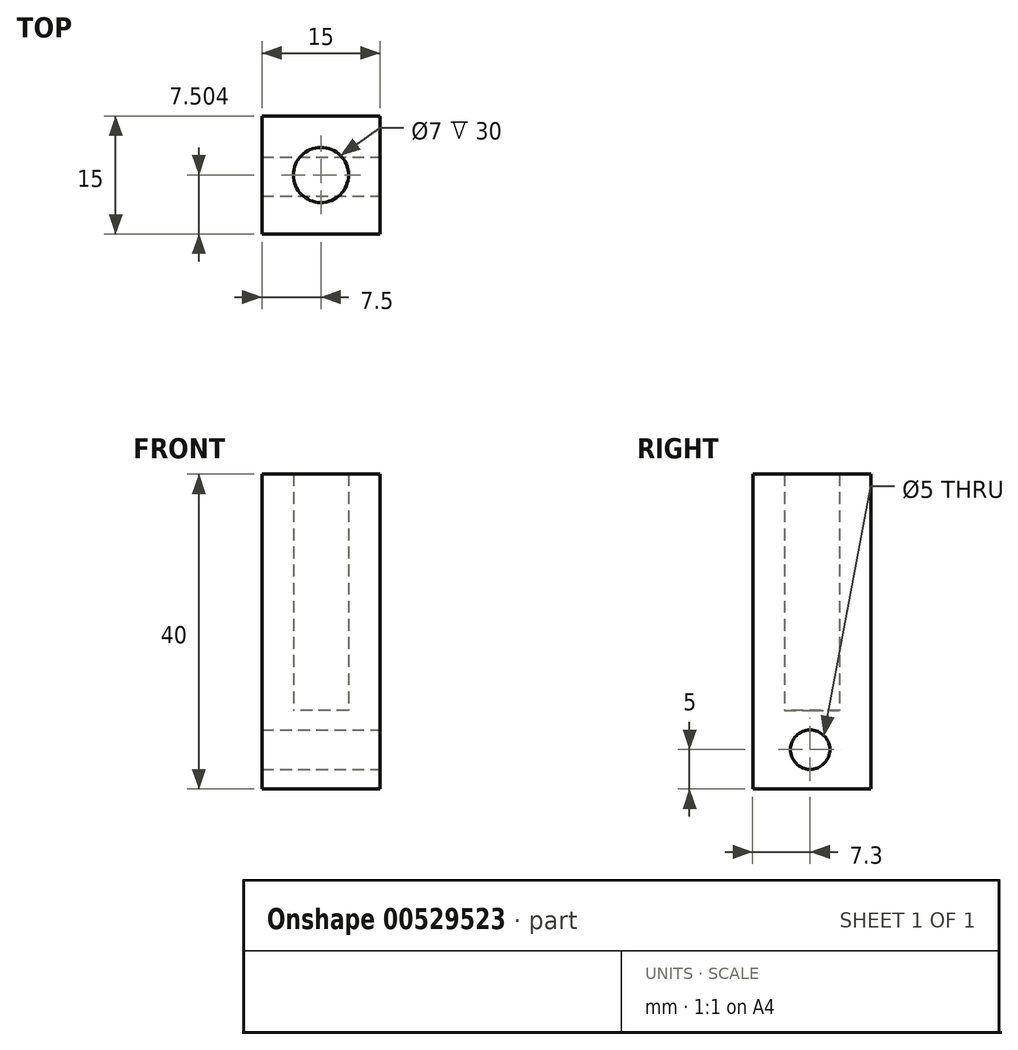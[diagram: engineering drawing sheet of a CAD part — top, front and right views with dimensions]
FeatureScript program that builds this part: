
annotation { "Feature Type Name" : "Feature", "Feature Type Description" : "" }
export const myFeature = defineFeature(function(context is Context, id is Id, definition is map)
    precondition{}
    {
        {
            var Q0;
            Q0=qCreatedBy(makeId("Top.planeOp"),FACE);
            var sketch = newSketch(context, id + "F0", { "sketchPlane" : qUnion([Q0])});
            skLineSegment(sketch, "E0.bottom", {"start": v(-7.5, 7.7) * mm, "end": v(7.5, 7.7) * mm});
            skLineSegment(sketch, "E0.top", {"start": v(-7.5, -7.3) * mm, "end": v(7.5, -7.3) * mm});
            skLineSegment(sketch, "E0.left", {"start": v(-7.5, 7.7) * mm, "end": v(-7.5, -7.3) * mm});
            skLineSegment(sketch, "E0.right", {"start": v(7.5, 7.7) * mm, "end": v(7.5, -7.3) * mm});
            skLineSegment(sketch, "E1", {"start": v(-7.5, -7.3) * mm, "end": v(-7.5, 0.2) * mm});
            skLineSegment(sketch, "E2", {"start": v(7.5, -7.3) * mm, "end": v(7.5, 0.2) * mm});
            skLineSegment(sketch, "E3", {"start": v(7.5, 0.2) * mm, "end": v(-7.5, 0.2) * mm});
            skLineSegment(sketch, "E4", {"start": v(-7.5, -7.3) * mm, "end": v(0, -7.3) * mm});
            skLineSegment(sketch, "E5", {"start": v(-7.5, 7.7) * mm, "end": v(0, 7.7) * mm});
            skLineSegment(sketch, "E6", {"start": v(0, 7.7) * mm, "end": v(0, -7.3) * mm});
            skCircle(sketch, "E7", {"center": v(0, 0.2) * mm, "radius": 3.5 * mm});
            skSolve(sketch);
        }
        {
            var Q0;
            {var subQ1=sQuery(id+"F0.wireOp",EDGE,"E0.bottom");Q0=makeQuery(id+"F0.imprint","IMPRINT",FACE,{"disambiguationData":[TD([[makeQuery(id+"F0.imprint","IMPRINT",EDGE,{"derivedFrom":subQ1}),-1.0]])]});}
            var Q1;
            {var subQ2=sQuery(id+"F0.wireOp",EDGE,"E0.left");Q1=makeQuery(id+"F0.imprint","IMPRINT",FACE,{"disambiguationData":[TD([[makeQuery(id+"F0.imprint","IMPRINT",EDGE,{"derivedFrom":subQ2}),1.0]])]});}
            var Q2;
            {var subQ4=sQuery(id+"F0.wireOp",EDGE,"E1");Q2=makeQuery(id+"F0.imprint","IMPRINT",FACE,{"disambiguationData":[TD([[makeQuery(id+"F0.imprint","IMPRINT",EDGE,{"derivedFrom":subQ4}),-1.0]])]});}
            var Q3;
            {var subQ1=sQuery(id+"F0.wireOp",EDGE,"E0.top");Q3=makeQuery(id+"F0.imprint","IMPRINT",FACE,{"disambiguationData":[TD([[makeQuery(id+"F0.imprint","IMPRINT",EDGE,{"derivedFrom":subQ1}),1.0]])]});}
            var Q4;
            {var subQ0=sQuery(id+"F0.wireOp",EDGE,"E6");var subQ1=sQuery(id+"F0.wireOp",EDGE,"E3");var subQ2=makeQuery(id+"F0.imprint","INTERSECT",VERTEX,{"derivedFrom":[subQ1,subQ0]});Q4=makeQuery(id+"F0.imprint","IMPRINT",FACE,{"disambiguationData":[TD([[makeQuery(id+"F0.imprint","IMPRINT",EDGE,{"disambiguationData":[TD([[subQ2,-1.0]])],"derivedFrom":subQ1}),-1.0]])]});}
            var Q5;
            {var subQ0=sQuery(id+"F0.wireOp",EDGE,"E7");var subQ1=sQuery(id+"F0.wireOp",EDGE,"E3");var subQ2=makeQuery(id+"F0.imprint","INTERSECT",VERTEX,{"disambiguationData":[OD(0.0)],"derivedFrom":[subQ1,subQ0]});Q5=makeQuery(id+"F0.imprint","IMPRINT",FACE,{"disambiguationData":[TD([[makeQuery(id+"F0.imprint","IMPRINT",EDGE,{"disambiguationData":[TD([[subQ2,-1.0]])],"derivedFrom":subQ1}),-1.0]])]});}
            var Q6;
            {var subQ0=sQuery(id+"F0.wireOp",EDGE,"E7");var subQ1=sQuery(id+"F0.wireOp",EDGE,"E3");var subQ2=makeQuery(id+"F0.imprint","INTERSECT",VERTEX,{"disambiguationData":[OD(0.0)],"derivedFrom":[subQ1,subQ0]});Q6=makeQuery(id+"F0.imprint","IMPRINT",FACE,{"disambiguationData":[TD([[makeQuery(id+"F0.imprint","IMPRINT",EDGE,{"disambiguationData":[TD([[subQ2,-1.0]])],"derivedFrom":subQ1}),1.0]])]});}
            var Q7;
            {var subQ0=sQuery(id+"F0.wireOp",EDGE,"E6");var subQ1=sQuery(id+"F0.wireOp",EDGE,"E3");var subQ2=makeQuery(id+"F0.imprint","INTERSECT",VERTEX,{"derivedFrom":[subQ1,subQ0]});Q7=makeQuery(id+"F0.imprint","IMPRINT",FACE,{"disambiguationData":[TD([[makeQuery(id+"F0.imprint","IMPRINT",EDGE,{"disambiguationData":[TD([[subQ2,-1.0]])],"derivedFrom":subQ1}),1.0]])]});}
            extrude(context, id + "F1", {"entities" : qUnion([Q0, Q1, Q2, Q3, Q4, Q5, Q6, Q7]), "depth" : 10 * mm, "offsetDistance" : 25 * mm});
        }
        {
            var Q0;
            Q0 = qSketchRegion(id + "F0", true);
            extrude(context, id + "F2", {"entities" : qUnion([Q0]), "operationType" : NewBodyOperationType.ADD, "depth" : 40 * mm, "offsetDistance" : 25 * mm});
        }
        {
            var Q0;
            {var subQ0=sQuery(id+"F0.wireOp",EDGE,"E2");var subQ1=sQuery(id+"F0.wireOp",EDGE,"E0.right");Q0=makeQuery(id+"F2.boolean.opBoolean","MERGE",FACE,{"derivedFrom":[makeQuery(id+"F1.opExtrude","SWEPT_FACE",FACE,{"disambiguationData":[OSD([subQ1,subQ0])]}),makeQuery(id+"F2.opExtrude","SWEPT_FACE",FACE,{"disambiguationData":[OSD([subQ1,subQ0])]})]});}
            var sketch = newSketch(context, id + "F3", { "sketchPlane" : qUnion([Q0])});
            skLineSegment(sketch, "E8", {"start": v(0, 0) * mm, "end": v(0, 10) * mm});
            skLineSegment(sketch, "E9", {"start": v(0, 10) * mm, "end": v(0, 5) * mm});
            skCircle(sketch, "E10", {"center": v(0, 5) * mm, "radius": 2.5 * mm});
            skSolve(sketch);
        }
        {
            var Q0;
            Q0 = qSketchRegion(id + "F3", true);
            extrude(context, id + "F4", {"entities" : qUnion([Q0]), "operationType" : NewBodyOperationType.REMOVE, "oppositeDirection" : true, "depth" : 15 * mm, "offsetDistance" : 25 * mm});
        }
    });
